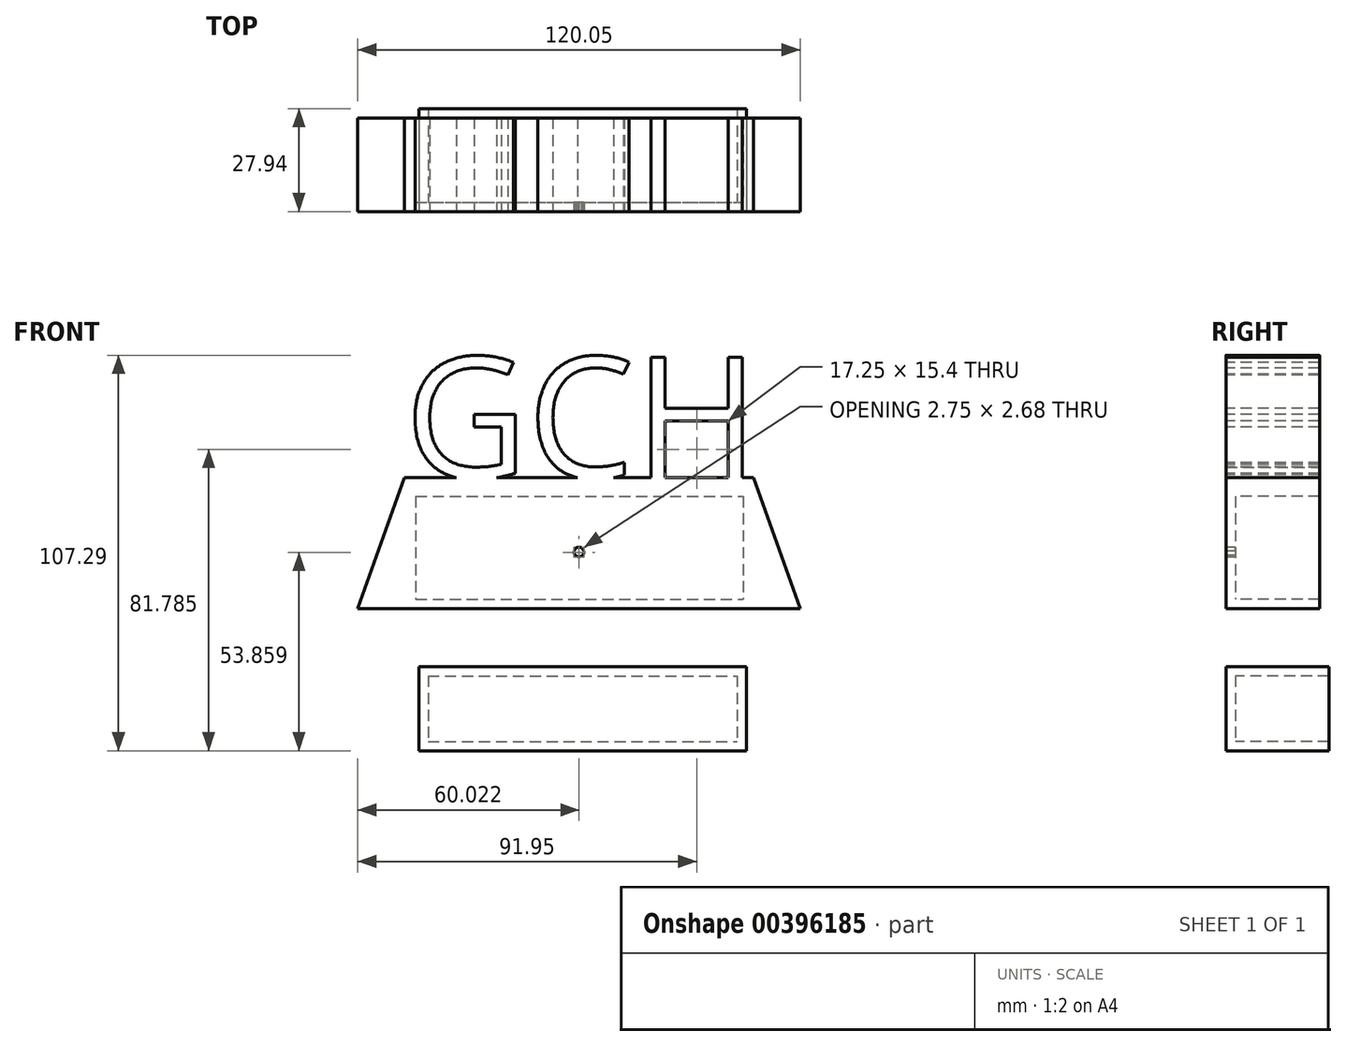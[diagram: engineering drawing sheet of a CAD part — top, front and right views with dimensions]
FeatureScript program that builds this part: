
annotation { "Feature Type Name" : "Feature", "Feature Type Description" : "" }
export const myFeature = defineFeature(function(context is Context, id is Id, definition is map)
    precondition{}
    {
        {
            var Q0;
            Q0=qCreatedBy(makeId("Front.planeOp"),FACE);
            var sketch = newSketch(context, id + "F0", { "sketchPlane" : qUnion([Q0])});
            skText(sketch, "E0", { "text": "GCH", "fontName": "OpenSans-Regular.ttf"});
            skLineSegment(sketch, "E1", {"start": v(-50.68, 8.82) * mm, "end": v(43.97, 8.82) * mm});
            skLineSegment(sketch, "E2", {"start": v(-50.68, -26.74) * mm, "end": v(43.97, -26.74) * mm});
            skLineSegment(sketch, "E3", {"start": v(43.97, -26.74) * mm, "end": v(56.67, -26.74) * mm});
            skLineSegment(sketch, "E4", {"start": v(43.97, 8.82) * mm, "end": v(56.67, -26.74) * mm});
            skLineSegment(sketch, "E5", {"start": v(-50.68, -26.74) * mm, "end": v(-63.38, -26.74) * mm});
            skLineSegment(sketch, "E6", {"start": v(-50.68, 8.82) * mm, "end": v(-63.38, -26.74) * mm});
            skLineSegment(sketch, "E7.top", {"start": v(-47.63, -24.16) * mm, "end": v(41.27, -24.16) * mm});
            skLineSegment(sketch, "E7.left", {"start": v(-47.63, 3.78) * mm, "end": v(-47.63, -24.16) * mm});
            skLineSegment(sketch, "E7.right", {"start": v(41.27, 3.78) * mm, "end": v(41.27, -24.16) * mm});
            skLineSegment(sketch, "E8", {"start": v(-47.63, 3.78) * mm, "end": v(41.27, 3.78) * mm});
            skCircle(sketch, "E9.cCircle", {"center": v(-3.36, -11.33) * mm, "radius": 1.27 * mm, "construction": true});
            skLineSegment(sketch, "E9.0", {"start": v(-3.97, -10.06) * mm, "end": v(-2.75, -10.06) * mm});
            skLineSegment(sketch, "E9.1", {"start": v(-2.75, -10.06) * mm, "end": v(-1.98, -11.02) * mm});
            skLineSegment(sketch, "E9.2", {"start": v(-1.98, -11.02) * mm, "end": v(-2.26, -12.21) * mm});
            skLineSegment(sketch, "E9.3", {"start": v(-2.26, -12.21) * mm, "end": v(-3.36, -12.74) * mm});
            skLineSegment(sketch, "E9.4", {"start": v(-3.36, -12.74) * mm, "end": v(-4.46, -12.21) * mm});
            skLineSegment(sketch, "E9.5", {"start": v(-4.46, -12.21) * mm, "end": v(-4.73, -11.02) * mm});
            skLineSegment(sketch, "E9.6", {"start": v(-4.73, -11.02) * mm, "end": v(-3.97, -10.06) * mm});
            skPoint(sketch, "E9.0.midPoint", {"position": v(-3.36, -10.06) * mm});
            const initialGuessF0  = {"E0": [-0.05068, 0.00882, 1, 0, 0.03302]};
            skSetInitialGuess(sketch, initialGuessF0);
            skSolve(sketch);
        }
        {
            var Q0;
            Q0 = qSketchRegion(id + "F0", true);
            extrude(context, id + "F1", {"entities" : qUnion([Q0]), "oppositeDirection" : true, "depth" : 25.4 * mm, "offsetDistance" : 25.4 * mm});
        }
        {
            var Q0;
            Q0=makeQuery(id+"F0.imprint","IMPRINT",FACE,{"disambiguationData":[TD([[makeQuery(id+"F0.imprint","IMPRINT",EDGE,{"derivedFrom":sQuery(id+"F0.wireOp",EDGE,"E7.top")}),1.0]])]});
            extrude(context, id + "F2", {"entities" : qUnion([Q0]), "operationType" : NewBodyOperationType.ADD, "oppositeDirection" : true, "depth" : 2.54 * mm, "offsetDistance" : 25.4 * mm});
        }
        {
            var Q0;
            Q0=qCreatedBy(makeId("Front.planeOp"),FACE);
            var sketch = newSketch(context, id + "F3", { "sketchPlane" : qUnion([Q0])});
            skLineSegment(sketch, "E10.bottom", {"start": v(-46.85, -42.4) * mm, "end": v(42.05, -42.4) * mm});
            skLineSegment(sketch, "E10.top", {"start": v(-46.85, -65.26) * mm, "end": v(42.05, -65.26) * mm});
            skLineSegment(sketch, "E10.left", {"start": v(-46.85, -42.4) * mm, "end": v(-46.85, -65.26) * mm});
            skLineSegment(sketch, "E10.right", {"start": v(42.05, -42.4) * mm, "end": v(42.05, -65.26) * mm});
            skLineSegment(sketch, "E11.0", {"start": v(-44.3, -44.94) * mm, "end": v(39.51, -44.94) * mm});
            skLineSegment(sketch, "E12.0", {"start": v(-44.3, -44.94) * mm, "end": v(-44.3, -62.72) * mm});
            skLineSegment(sketch, "E13.0", {"start": v(-44.3, -62.72) * mm, "end": v(39.51, -62.72) * mm});
            skLineSegment(sketch, "E14.0", {"start": v(39.51, -44.94) * mm, "end": v(39.51, -62.72) * mm});
            skSolve(sketch);
        }
        {
            var Q0;
            Q0 = qSketchRegion(id + "F3", true);
            extrude(context, id + "F4", {"entities" : qUnion([Q0]), "oppositeDirection" : true, "depth" : 27.94 * mm, "offsetDistance" : 25.4 * mm});
        }
        {
            var Q0;
            Q0=makeQuery(id+"F3.imprint","IMPRINT",FACE,{"disambiguationData":[TD([[makeQuery(id+"F3.imprint","IMPRINT",EDGE,{"derivedFrom":sQuery(id+"F3.wireOp",EDGE,"E11.0")}),-1.0]])]});
            extrude(context, id + "F5", {"entities" : qUnion([Q0]), "operationType" : NewBodyOperationType.ADD, "oppositeDirection" : true, "depth" : 2.54 * mm, "offsetDistance" : 25.4 * mm});
        }
    });
